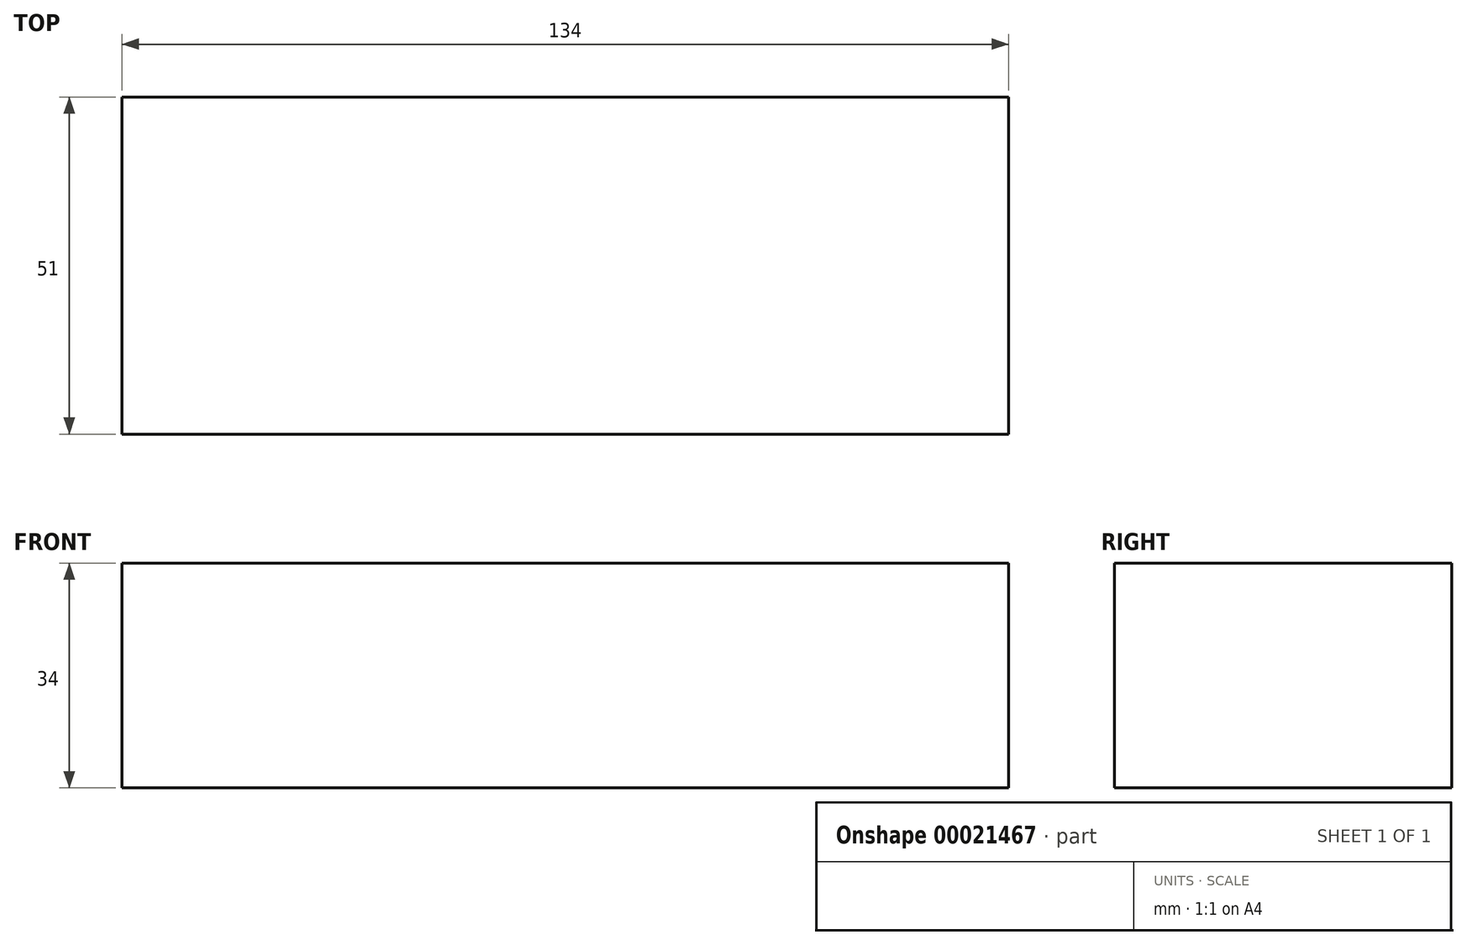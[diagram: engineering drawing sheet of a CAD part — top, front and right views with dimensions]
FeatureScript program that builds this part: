
annotation { "Feature Type Name" : "Feature", "Feature Type Description" : "" }
export const myFeature = defineFeature(function(context is Context, id is Id, definition is map)
    precondition{}
    {
        {
            var Q0;
            Q0=qCreatedBy(makeId("Top.planeOp"),FACE);
            var sketch = newSketch(context, id + "F0", { "sketchPlane" : qUnion([Q0])});
            skLineSegment(sketch, "E0.rect.bottom", {"start": v(67, -25.5) * mm, "end": v(-67, -25.5) * mm});
            skLineSegment(sketch, "E0.rect.top", {"start": v(67, 25.5) * mm, "end": v(-67, 25.5) * mm});
            skLineSegment(sketch, "E0.rect.left", {"start": v(67, -25.5) * mm, "end": v(67, 25.5) * mm});
            skLineSegment(sketch, "E0.rect.right", {"start": v(-67, -25.5) * mm, "end": v(-67, 25.5) * mm});
            skPoint(sketch, "E0.rect.middle", {"position": v(0, 0) * mm});
            skSolve(sketch);
        }
        {
            var Q0;
            Q0 = qSketchRegion(id + "F0", true);
            extrude(context, id + "F1", {"entities" : qUnion([Q0]), "depth" : 34 * mm});
        }
    });
